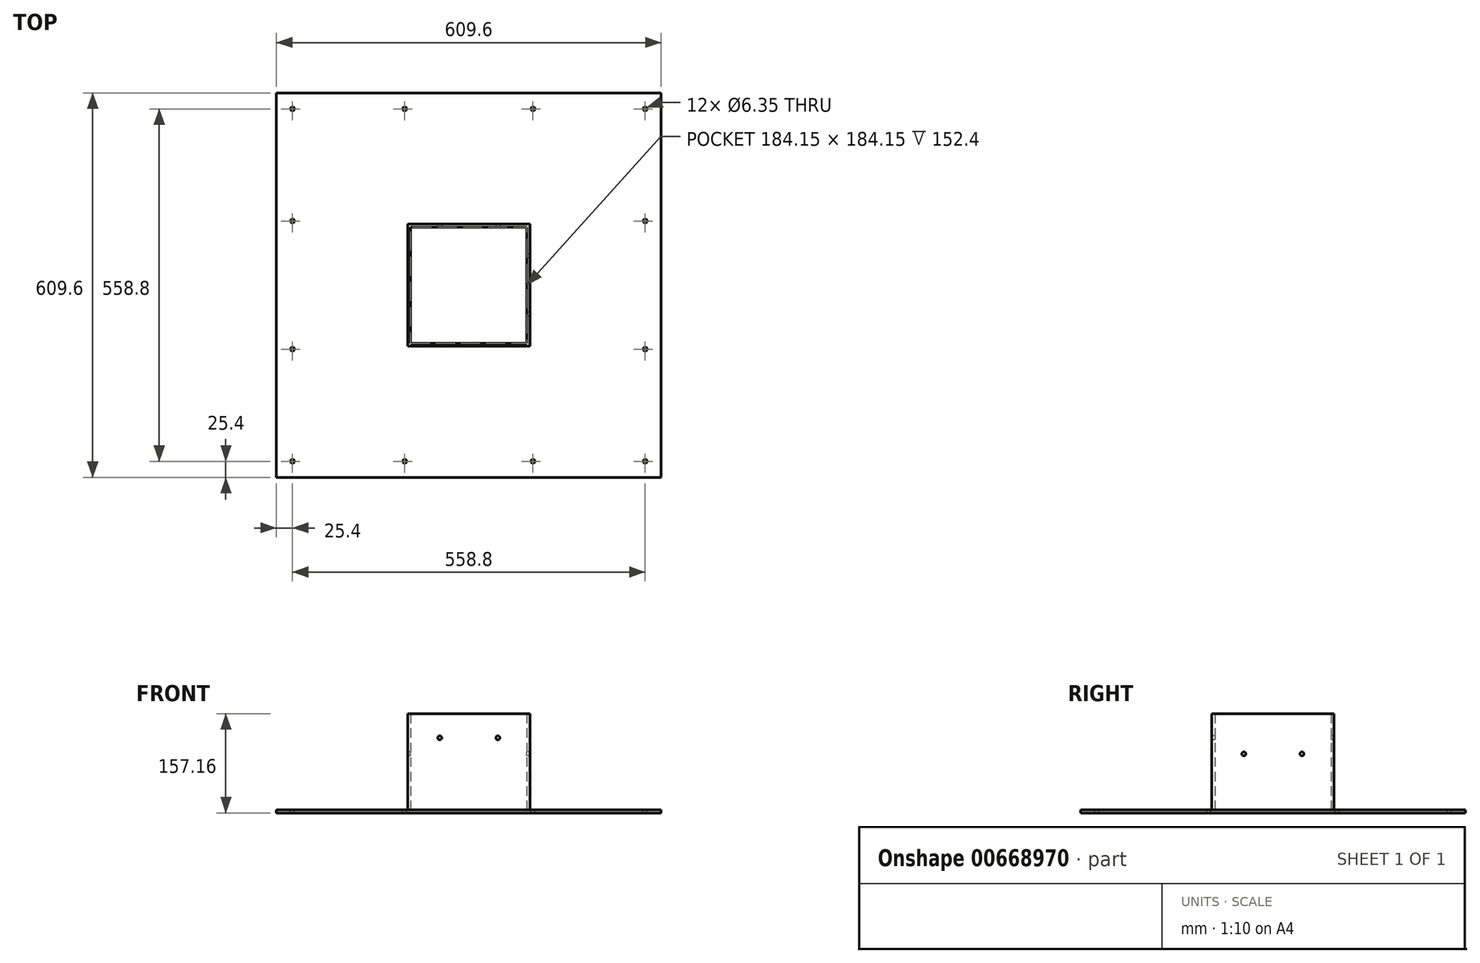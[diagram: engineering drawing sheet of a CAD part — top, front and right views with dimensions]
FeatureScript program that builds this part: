
annotation { "Feature Type Name" : "Feature", "Feature Type Description" : "" }
export const myFeature = defineFeature(function(context is Context, id is Id, definition is map)
    precondition{}
    {
        {
            var Q0;
            Q0=qCreatedBy(makeId("Top.planeOp"),FACE);
            var sketch = newSketch(context, id + "F0", { "sketchPlane" : qUnion([Q0])});
            skLineSegment(sketch, "E0.bottom", {"start": v(-609.6, 609.6) * mm, "end": v(0, 609.6) * mm});
            skLineSegment(sketch, "E0.top", {"start": v(-609.6, 0) * mm, "end": v(0, 0) * mm});
            skLineSegment(sketch, "E0.left", {"start": v(-609.6, 609.6) * mm, "end": v(-609.6, 0) * mm});
            skLineSegment(sketch, "E0.right", {"start": v(0, 609.6) * mm, "end": v(0, 0) * mm});
            skSolve(sketch);
        }
        {
            var Q0;
            Q0 = qSketchRegion(id + "F0", true);
            extrude(context, id + "F1", {"entities" : qUnion([Q0]), "depth" : 4.76 * mm, "offsetDistance" : 25.4 * mm});
        }
        {
            var Q0;
            Q0=makeQuery(id+"F1.opExtrude","CAP_FACE",FACE,{"disambiguationData":[OSD([sQuery(id+"F0.wireOp",EDGE,"E0.bottom"),sQuery(id+"F0.wireOp",EDGE,"E0.top"),sQuery(id+"F0.wireOp",EDGE,"E0.left"),sQuery(id+"F0.wireOp",EDGE,"E0.right")])],"isStart":false});
            var sketch = newSketch(context, id + "F2", { "sketchPlane" : qUnion([Q0])});
            skLineSegment(sketch, "E1.bottom", {"start": v(-401.64, 401.64) * mm, "end": v(-207.96, 401.64) * mm});
            skLineSegment(sketch, "E1.top", {"start": v(-401.64, 207.96) * mm, "end": v(-207.96, 207.96) * mm});
            skLineSegment(sketch, "E1.left", {"start": v(-401.64, 401.64) * mm, "end": v(-401.64, 207.96) * mm});
            skLineSegment(sketch, "E1.right", {"start": v(-207.96, 401.64) * mm, "end": v(-207.96, 207.96) * mm});
            skLineSegment(sketch, "E2.bottom", {"start": v(-396.88, 396.88) * mm, "end": v(-212.72, 396.88) * mm});
            skLineSegment(sketch, "E2.top", {"start": v(-396.88, 212.72) * mm, "end": v(-212.72, 212.72) * mm});
            skLineSegment(sketch, "E2.left", {"start": v(-396.88, 396.88) * mm, "end": v(-396.88, 212.72) * mm});
            skLineSegment(sketch, "E2.right", {"start": v(-212.72, 396.88) * mm, "end": v(-212.72, 212.72) * mm});
            skSolve(sketch);
        }
        {
            var Q0;
            Q0 = qSketchRegion(id + "F2", true);
            extrude(context, id + "F3", {"entities" : qUnion([Q0]), "operationType" : NewBodyOperationType.ADD, "depth" : 152.4 * mm, "offsetDistance" : 25.4 * mm});
        }
        {
            var Q0;
            {var subQ0=sQuery(id+"F0.wireOp",EDGE,"E0.left");var subQ1=sQuery(id+"F0.wireOp",EDGE,"E0.top");var subQ2=sQuery(id+"F0.wireOp",EDGE,"E0.right");var subQ3=sQuery(id+"F0.wireOp",EDGE,"E0.bottom");Q0=makeQuery(id+"F3.boolean.opBoolean","SPLIT",FACE,{"disambiguationData":[TD([makeQuery(id+"F1.opExtrude","SWEPT_FACE",FACE,{"disambiguationData":[OSD([subQ3])]})])],"derivedFrom":makeQuery(id+"F1.opExtrude","CAP_FACE",FACE,{"disambiguationData":[OSD([subQ3,subQ1,subQ0,subQ2])],"isStart":false})});}
            var sketch = newSketch(context, id + "F4", { "sketchPlane" : qUnion([Q0])});
            skCircle(sketch, "E3", {"center": v(-25.4, 584.2) * mm, "radius": 3.18 * mm});
            skCircle(sketch, "E4.0.1.0", {"center": v(-25.4, 25.4) * mm, "radius": 3.18 * mm});
            skCircle(sketch, "E4.1.0.0", {"center": v(-584.2, 584.2) * mm, "radius": 3.18 * mm});
            skCircle(sketch, "E4.1.1.0", {"center": v(-584.2, 25.4) * mm, "radius": 3.18 * mm});
            skLineSegment(sketch, "E4.direction1", {"start": v(-25.4, 584.2) * mm, "end": v(-584.2, 584.2) * mm, "construction": true});
            skLineSegment(sketch, "E4.direction2", {"start": v(-25.4, 584.2) * mm, "end": v(-25.4, 25.4) * mm, "construction": true});
            skCircle(sketch, "E5", {"center": v(-25.4, 406.4) * mm, "radius": 3.18 * mm});
            skCircle(sketch, "E6.0.1.0", {"center": v(-25.4, 203.2) * mm, "radius": 3.18 * mm});
            skCircle(sketch, "E6.1.0.0", {"center": v(-584.2, 406.4) * mm, "radius": 3.18 * mm});
            skCircle(sketch, "E6.1.1.0", {"center": v(-584.2, 203.2) * mm, "radius": 3.18 * mm});
            skLineSegment(sketch, "E6.direction1", {"start": v(-25.4, 406.4) * mm, "end": v(-584.2, 406.4) * mm, "construction": true});
            skLineSegment(sketch, "E6.direction2", {"start": v(-25.4, 406.4) * mm, "end": v(-25.4, 203.2) * mm, "construction": true});
            skCircle(sketch, "E7", {"center": v(-406.4, 25.4) * mm, "radius": 3.17 * mm});
            skCircle(sketch, "E8.0.1.0", {"center": v(-406.4, 584.2) * mm, "radius": 3.17 * mm});
            skCircle(sketch, "E8.1.0.0", {"center": v(-203.2, 25.4) * mm, "radius": 3.17 * mm});
            skCircle(sketch, "E8.1.1.0", {"center": v(-203.2, 584.2) * mm, "radius": 3.17 * mm});
            skLineSegment(sketch, "E8.direction1", {"start": v(-406.4, 25.4) * mm, "end": v(-203.2, 25.4) * mm, "construction": true});
            skLineSegment(sketch, "E8.direction2", {"start": v(-406.4, 25.4) * mm, "end": v(-406.4, 584.2) * mm, "construction": true});
            skSolve(sketch);
        }
        {
            var Q0;
            Q0 = qSketchRegion(id + "F4", true);
            extrude(context, id + "F5", {"entities" : qUnion([Q0]), "operationType" : NewBodyOperationType.REMOVE, "oppositeDirection" : true, "depth" : 25.4 * mm, "offsetDistance" : 25.4 * mm});
        }
        {
            var Q0;
            Q0=makeQuery(id+"F3.opExtrude","SWEPT_FACE",FACE,{"disambiguationData":[OSD([sQuery(id+"F2.wireOp",EDGE,"E1.top")])]});
            var sketch = newSketch(context, id + "F6", { "sketchPlane" : qUnion([Q0])});
            skCircle(sketch, "E9", {"center": v(-350.84, 119.06) * mm, "radius": 3.18 * mm});
            skCircle(sketch, "E10", {"center": v(-258.76, 119.06) * mm, "radius": 3.18 * mm});
            skSolve(sketch);
        }
        {
            var Q0;
            Q0 = qSketchRegion(id + "F6", true);
            extrude(context, id + "F7", {"entities" : qUnion([Q0]), "operationType" : NewBodyOperationType.REMOVE, "endBound" : BoundingType.THROUGH_ALL, "oppositeDirection" : true, "depth" : 25.4 * mm, "offsetDistance" : 25.4 * mm});
        }
        {
            var Q0;
            Q0=makeQuery(id+"F3.opExtrude","SWEPT_FACE",FACE,{"disambiguationData":[OSD([sQuery(id+"F2.wireOp",EDGE,"E1.left")])]});
            var sketch = newSketch(context, id + "F8", { "sketchPlane" : qUnion([Q0])});
            skCircle(sketch, "E11", {"center": v(-258.76, 93.66) * mm, "radius": 3.18 * mm});
            skCircle(sketch, "E12", {"center": v(-350.84, 93.66) * mm, "radius": 3.18 * mm});
            skSolve(sketch);
        }
        {
            var Q0;
            Q0 = qSketchRegion(id + "F8", true);
            extrude(context, id + "F9", {"entities" : qUnion([Q0]), "operationType" : NewBodyOperationType.REMOVE, "endBound" : BoundingType.THROUGH_ALL, "oppositeDirection" : true, "depth" : 25.4 * mm, "offsetDistance" : 25.4 * mm});
        }
    });
